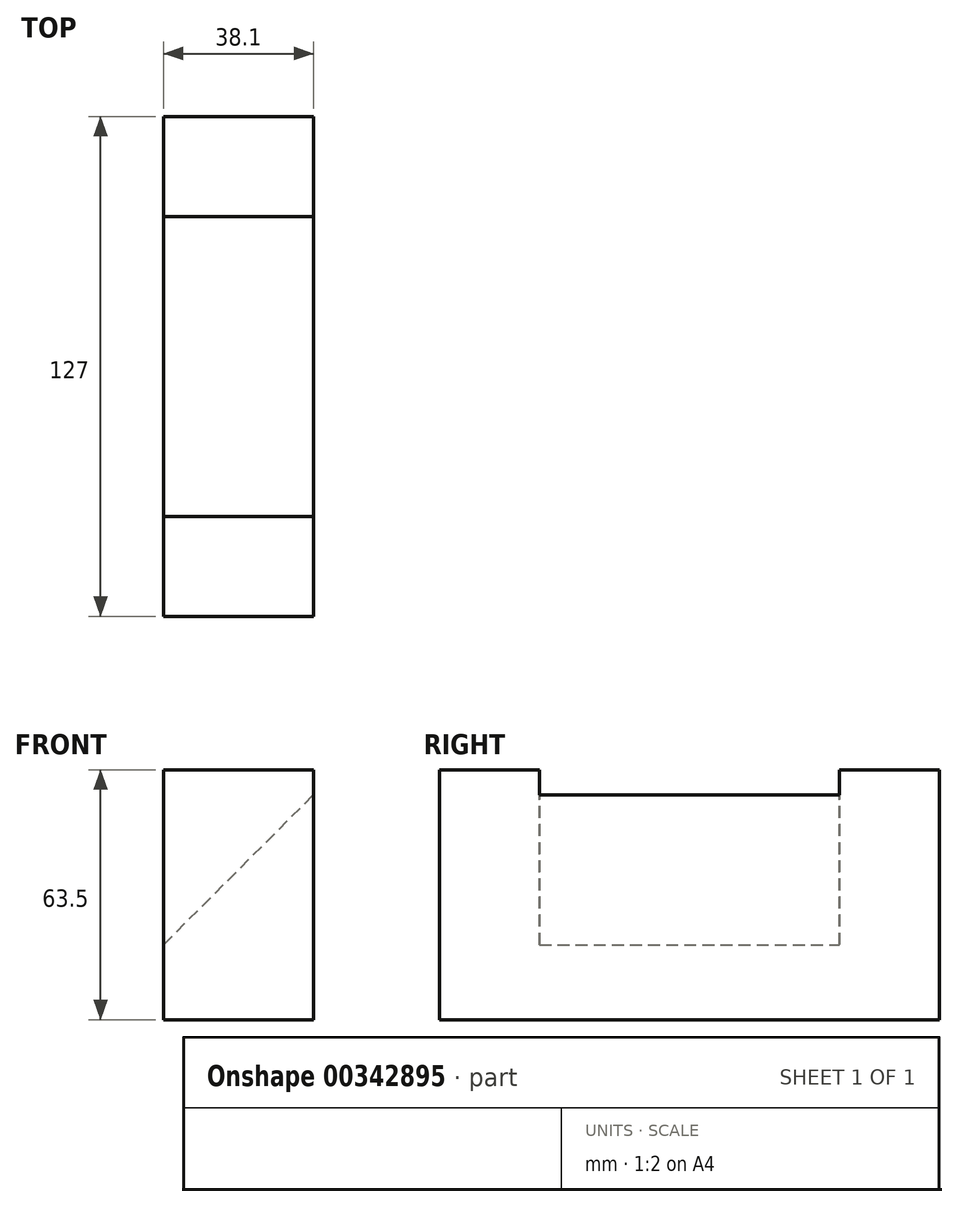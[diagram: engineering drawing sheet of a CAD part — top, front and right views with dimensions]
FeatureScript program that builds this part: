
annotation { "Feature Type Name" : "Feature", "Feature Type Description" : "" }
export const myFeature = defineFeature(function(context is Context, id is Id, definition is map)
    precondition{}
    {
        {
            var Q0;
            Q0=qCreatedBy(makeId("Front.planeOp"),FACE);
            var sketch = newSketch(context, id + "F0", { "sketchPlane" : qUnion([Q0])});
            skLineSegment(sketch, "E0", {"start": v(-47.02, -21.4) * mm, "end": v(-8.92, -21.4) * mm});
            skLineSegment(sketch, "E1", {"start": v(-8.92, -21.4) * mm, "end": v(-8.92, 42.1) * mm});
            skLineSegment(sketch, "E2", {"start": v(-8.92, 42.1) * mm, "end": v(-47.02, 42.1) * mm});
            skLineSegment(sketch, "E3", {"start": v(-47.02, 42.1) * mm, "end": v(-47.02, -21.4) * mm});
            skLineSegment(sketch, "E4", {"start": v(-47.02, -21.4) * mm, "end": v(-47.02, -2.35) * mm});
            skLineSegment(sketch, "E5", {"start": v(-47.02, -2.35) * mm, "end": v(-8.92, 35.75) * mm});
            skSolve(sketch);
        }
        {
            var Q0;
            {var subQ0=sQuery(id+"F0.wireOp",EDGE,"E0");Q0=makeQuery(id+"F0.imprint","IMPRINT",FACE,{"disambiguationData":[TD([[makeQuery(id+"F0.imprint","IMPRINT",EDGE,{"derivedFrom":subQ0}),1.0]])]});}
            extrude(context, id + "F1", {"entities" : qUnion([Q0]), "depth" : 63.5 * mm});
        }
        {
            var Q0;
            {var subQ0=sQuery(id+"F0.wireOp",EDGE,"E2");Q0=makeQuery(id+"F0.imprint","IMPRINT",FACE,{"disambiguationData":[TD([[makeQuery(id+"F0.imprint","IMPRINT",EDGE,{"derivedFrom":subQ0}),1.0]])]});}
            extrude(context, id + "F2", {"entities" : qUnion([Q0]), "operationType" : NewBodyOperationType.ADD, "depth" : 25.4 * mm});
        }
        {
            var Q0;
            Q0=makeQuery(id+"F1.opExtrude","SWEPT_BODY",BODY,{"disambiguationData":[OSD([sQuery(id+"F0.wireOp",EDGE,"E0"),sQuery(id+"F0.wireOp",EDGE,"E1"),sQuery(id+"F0.wireOp",EDGE,"E4"),sQuery(id+"F0.wireOp",EDGE,"E5")])]});
            var Q1;
            Q1=makeQuery(id+"F1.opExtrude","CAP_FACE",FACE,{"disambiguationData":[OSD([sQuery(id+"F0.wireOp",EDGE,"E0"),sQuery(id+"F0.wireOp",EDGE,"E1"),sQuery(id+"F0.wireOp",EDGE,"E4"),sQuery(id+"F0.wireOp",EDGE,"E5")])],"isStart":false});
            mirror(context, id + "F3", {"operationType" : NewBodyOperationType.ADD, "entities" : qUnion([Q0]), "mirrorPlane" : qUnion([Q1])});
        }
    });
